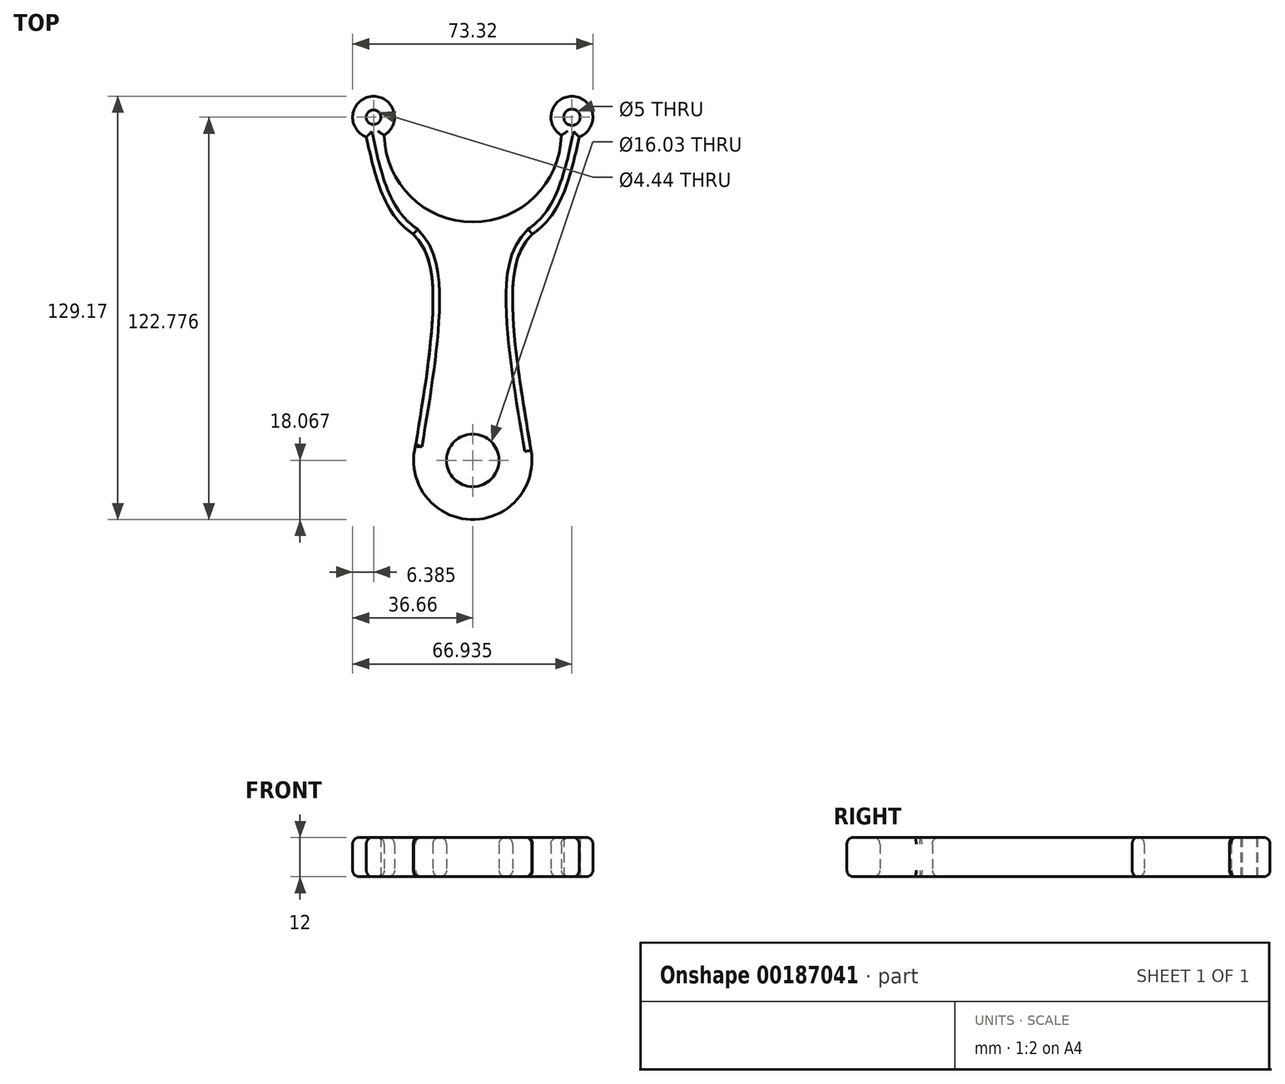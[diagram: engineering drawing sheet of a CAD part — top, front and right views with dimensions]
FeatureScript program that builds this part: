
annotation { "Feature Type Name" : "Feature", "Feature Type Description" : "" }
export const myFeature = defineFeature(function(context is Context, id is Id, definition is map)
    precondition{}
    {
        {
            var Q0;
            Q0=qCreatedBy(makeId("Top.planeOp"),FACE);
            var sketch = newSketch(context, id + "F0", { "sketchPlane" : qUnion([Q0])});
            skArc(sketch, "E0", {"start": v(-27, 0) * mm, "mid": v(-0.25, -27) * mm, "end": v(27, -0.5) * mm});
            skLineSegment(sketch, "E1", {"start": v(0, 0) * mm, "end": v(0, 27) * mm, "construction": true});
            skLineSegment(sketch, "E2", {"start": v(0, 0) * mm, "end": v(0, -27) * mm, "construction": true});
            skLineSegment(sketch, "E3", {"start": v(0, 0) * mm, "end": v(-27, 0) * mm});
            skLineSegment(sketch, "E4", {"start": v(-27, 0) * mm, "end": v(27, 0) * mm, "construction": true});
            skFitSpline(sketch, "E5", {"points": [v(0, -38.66) * mm, v(22.6, -26.79) * mm, v(32.7, 0) * mm], "startDerivative": vector(53.05, 17.73) * mm, "endDerivative": vector(12.73, 59.18) * mm});
            skFitSpline(sketch, "E6.MirrorCS", {"points": [v(0, -38.66) * mm, v(-22.6, -26.79) * mm, v(-32.7, 0) * mm], "startDerivative": vector(-53.05, 17.73) * mm, "endDerivative": vector(-12.73, 59.18) * mm});
            skArc(sketch, "E7", {"start": v(32.48, -1.01) * mm, "mid": v(30.87, 11.35) * mm, "end": v(27, -0.5) * mm});
            skArc(sketch, "E8", {"start": v(-17.48, -95.18) * mm, "mid": v(-0.76, -117.77) * mm, "end": v(17.8, -96.66) * mm});
            skArc(sketch, "E9.MirrorC", {"start": v(-32.48, -1.01) * mm, "mid": v(-30.87, 11.35) * mm, "end": v(-27, -0.5) * mm});
            skFitSpline(sketch, "E10", {"points": [v(22.6, -26.79) * mm, v(13.5, -38.66) * mm, v(17.82, -96.8) * mm], "startDerivative": vector(-32.69, -26.53) * mm, "endDerivative": vector(17.64, -104.94) * mm});
            skFitSpline(sketch, "E11", {"points": [v(-22.6, -26.79) * mm, v(-13.5, -38.66) * mm, v(-18, -98.3) * mm], "startDerivative": vector(32.95, -26.64) * mm, "endDerivative": vector(-18.1, -107.4) * mm});
            skCircle(sketch, "E12", {"center": v(0, -99.72) * mm, "radius": 8.02 * mm});
            skCircle(sketch, "E13", {"center": v(30.27, 4.99) * mm, "radius": 2.5 * mm});
            skCircle(sketch, "E14", {"center": v(-30.27, 4.99) * mm, "radius": 2.22 * mm});
            skSolve(sketch);
        }
        {
            var Q0;
            Q0 = qSketchRegion(id + "F0", true);
            extrude(context, id + "F1", {"entities" : qUnion([Q0]), "depth" : 12 * mm});
        }
        {
            var Q0;
            Q0=makeQuery(id+"F1.opExtrude","CAP_EDGE",EDGE,{"disambiguationData":[OSD([sQuery(id+"F0.wireOp",EDGE,"E10")])],"isStart":false});
            var Q1;
            Q1=makeQuery(id+"F1.opExtrude","CAP_EDGE",EDGE,{"disambiguationData":[OSD([sQuery(id+"F0.wireOp",EDGE,"E11")])],"isStart":false});
            var Q2;
            Q2=makeQuery(id+"F1.opExtrude","CAP_EDGE",EDGE,{"disambiguationData":[OSD([sQuery(id+"F0.wireOp",EDGE,"E8")])],"isStart":true});
            var Q3;
            Q3=makeQuery(id+"F1.opExtrude","CAP_EDGE",EDGE,{"disambiguationData":[OSD([sQuery(id+"F0.wireOp",EDGE,"E8")])],"isStart":false});
            var Q4;
            Q4=makeQuery(id+"F1.opExtrude","CAP_EDGE",EDGE,{"disambiguationData":[OSD([sQuery(id+"F0.wireOp",EDGE,"E0")])],"isStart":false});
            var Q5;
            Q5=makeQuery(id+"F1.opExtrude","CAP_EDGE",EDGE,{"disambiguationData":[OSD([sQuery(id+"F0.wireOp",EDGE,"E6.MirrorCS")])],"isStart":false});
            var Q6;
            Q6=makeQuery(id+"F1.opExtrude","CAP_EDGE",EDGE,{"disambiguationData":[OSD([sQuery(id+"F0.wireOp",EDGE,"E0")])],"isStart":true});
            var Q7;
            Q7=makeQuery(id+"F1.opExtrude","CAP_EDGE",EDGE,{"disambiguationData":[OSD([sQuery(id+"F0.wireOp",EDGE,"E5")])],"isStart":false});
            var Q8;
            Q8=makeQuery(id+"F1.opExtrude","CAP_EDGE",EDGE,{"disambiguationData":[OSD([sQuery(id+"F0.wireOp",EDGE,"E5")])],"isStart":true});
            var Q9;
            Q9=makeQuery(id+"F1.opExtrude","CAP_EDGE",EDGE,{"disambiguationData":[OSD([sQuery(id+"F0.wireOp",EDGE,"E10")])],"isStart":true});
            var Q10;
            Q10=makeQuery(id+"F1.opExtrude","CAP_EDGE",EDGE,{"disambiguationData":[OSD([sQuery(id+"F0.wireOp",EDGE,"E9.MirrorC")])],"isStart":false});
            var Q11;
            Q11=makeQuery(id+"F1.opExtrude","CAP_EDGE",EDGE,{"disambiguationData":[OSD([sQuery(id+"F0.wireOp",EDGE,"E9.MirrorC")])],"isStart":true});
            var Q12;
            Q12=makeQuery(id+"F1.opExtrude","CAP_EDGE",EDGE,{"disambiguationData":[OSD([sQuery(id+"F0.wireOp",EDGE,"E7")])],"isStart":false});
            var Q13;
            Q13=makeQuery(id+"F1.opExtrude","CAP_EDGE",EDGE,{"disambiguationData":[OSD([sQuery(id+"F0.wireOp",EDGE,"E7")])],"isStart":true});
            var Q14;
            Q14=makeQuery(id+"F1.opExtrude","CAP_EDGE",EDGE,{"disambiguationData":[OSD([sQuery(id+"F0.wireOp",EDGE,"E12")])],"isStart":false});
            var Q15;
            Q15=makeQuery(id+"F1.opExtrude","CAP_EDGE",EDGE,{"disambiguationData":[OSD([sQuery(id+"F0.wireOp",EDGE,"E12")])],"isStart":true});
            var Q16;
            Q16=makeQuery(id+"F1.opExtrude","CAP_EDGE",EDGE,{"disambiguationData":[OSD([sQuery(id+"F0.wireOp",EDGE,"E11")])],"isStart":true});
            var Q17;
            Q17=makeQuery(id+"F1.opExtrude","CAP_EDGE",EDGE,{"disambiguationData":[OSD([sQuery(id+"F0.wireOp",EDGE,"E6.MirrorCS")])],"isStart":true});
            fillet(context, id + "F2", {"entities" : qUnion([Q0, Q1, Q2, Q3, Q4, Q5, Q6, Q7, Q8, Q9, Q10, Q11, Q12, Q13, Q14, Q15, Q16, Q17]), "radius" : 2 * mm, "tangentPropagation" : true, "allowEdgeOverflow" : false});
        }
        {
            var Q0;
            {var subQ0=sQuery(id+"F0.wireOp",EDGE,"E10");Q0=makeQuery(id+"F2.opFillet","BLEND_EDGE",EDGE,{"blendedFrom":[makeQuery(id+"F1.opExtrude","CAP_EDGE",EDGE,{"disambiguationData":[OSD([subQ0])],"isStart":false}),makeQuery(id+"F1.opExtrude","CAP_FACE",FACE,{"disambiguationData":[OSD([sQuery(id+"F0.wireOp",EDGE,"E0"),sQuery(id+"F0.wireOp",EDGE,"E5"),sQuery(id+"F0.wireOp",EDGE,"E6.MirrorCS"),sQuery(id+"F0.wireOp",EDGE,"E7"),sQuery(id+"F0.wireOp",EDGE,"E8"),sQuery(id+"F0.wireOp",EDGE,"E9.MirrorC"),subQ0,sQuery(id+"F0.wireOp",EDGE,"E11"),sQuery(id+"F0.wireOp",EDGE,"E12"),sQuery(id+"F0.wireOp",EDGE,"E13"),sQuery(id+"F0.wireOp",EDGE,"E14")])],"isStart":false})],"blendedInto":[makeQuery(id+"F1.opExtrude","CAP_FACE",FACE,{"disambiguationData":[OSD([sQuery(id+"F0.wireOp",EDGE,"E0"),sQuery(id+"F0.wireOp",EDGE,"E5"),sQuery(id+"F0.wireOp",EDGE,"E6.MirrorCS"),sQuery(id+"F0.wireOp",EDGE,"E7"),sQuery(id+"F0.wireOp",EDGE,"E8"),sQuery(id+"F0.wireOp",EDGE,"E9.MirrorC"),subQ0,sQuery(id+"F0.wireOp",EDGE,"E11"),sQuery(id+"F0.wireOp",EDGE,"E12"),sQuery(id+"F0.wireOp",EDGE,"E13"),sQuery(id+"F0.wireOp",EDGE,"E14")])],"isStart":false})]});}
            var Q1;
            {var subQ0=sQuery(id+"F0.wireOp",EDGE,"E8");Q1=makeQuery(id+"F2.opFillet","BLEND_FACE",FACE,{"disambiguationData":[OSD([subQ0]),TDD([makeQuery(id+"F1.opExtrude","CAP_EDGE",EDGE,{"disambiguationData":[OSD([subQ0])],"isStart":false})])]});}
            var Q2;
            {var subQ0=sQuery(id+"F0.wireOp",EDGE,"E0");Q2=makeQuery(id+"F2.opFillet","BLEND_EDGE",EDGE,{"blendedFrom":[makeQuery(id+"F1.opExtrude","CAP_EDGE",EDGE,{"disambiguationData":[OSD([subQ0])],"isStart":false}),makeQuery(id+"F1.opExtrude","CAP_FACE",FACE,{"disambiguationData":[OSD([subQ0,sQuery(id+"F0.wireOp",EDGE,"E5"),sQuery(id+"F0.wireOp",EDGE,"E6.MirrorCS"),sQuery(id+"F0.wireOp",EDGE,"E7"),sQuery(id+"F0.wireOp",EDGE,"E8"),sQuery(id+"F0.wireOp",EDGE,"E9.MirrorC"),sQuery(id+"F0.wireOp",EDGE,"E10"),sQuery(id+"F0.wireOp",EDGE,"E11"),sQuery(id+"F0.wireOp",EDGE,"E12"),sQuery(id+"F0.wireOp",EDGE,"E13"),sQuery(id+"F0.wireOp",EDGE,"E14")])],"isStart":false})],"blendedInto":[makeQuery(id+"F1.opExtrude","CAP_FACE",FACE,{"disambiguationData":[OSD([subQ0,sQuery(id+"F0.wireOp",EDGE,"E5"),sQuery(id+"F0.wireOp",EDGE,"E6.MirrorCS"),sQuery(id+"F0.wireOp",EDGE,"E7"),sQuery(id+"F0.wireOp",EDGE,"E8"),sQuery(id+"F0.wireOp",EDGE,"E9.MirrorC"),sQuery(id+"F0.wireOp",EDGE,"E10"),sQuery(id+"F0.wireOp",EDGE,"E11"),sQuery(id+"F0.wireOp",EDGE,"E12"),sQuery(id+"F0.wireOp",EDGE,"E13"),sQuery(id+"F0.wireOp",EDGE,"E14")])],"isStart":false})]});}
            var Q3;
            {var subQ0=sQuery(id+"F0.wireOp",EDGE,"E11");Q3=makeQuery(id+"F2.opFillet","BLEND_EDGE",EDGE,{"blendedFrom":[makeQuery(id+"F1.opExtrude","CAP_EDGE",EDGE,{"disambiguationData":[OSD([subQ0])],"isStart":false}),makeQuery(id+"F1.opExtrude","CAP_FACE",FACE,{"disambiguationData":[OSD([sQuery(id+"F0.wireOp",EDGE,"E0"),sQuery(id+"F0.wireOp",EDGE,"E5"),sQuery(id+"F0.wireOp",EDGE,"E6.MirrorCS"),sQuery(id+"F0.wireOp",EDGE,"E7"),sQuery(id+"F0.wireOp",EDGE,"E8"),sQuery(id+"F0.wireOp",EDGE,"E9.MirrorC"),sQuery(id+"F0.wireOp",EDGE,"E10"),subQ0,sQuery(id+"F0.wireOp",EDGE,"E12"),sQuery(id+"F0.wireOp",EDGE,"E13"),sQuery(id+"F0.wireOp",EDGE,"E14")])],"isStart":false})],"blendedInto":[makeQuery(id+"F1.opExtrude","CAP_FACE",FACE,{"disambiguationData":[OSD([sQuery(id+"F0.wireOp",EDGE,"E0"),sQuery(id+"F0.wireOp",EDGE,"E5"),sQuery(id+"F0.wireOp",EDGE,"E6.MirrorCS"),sQuery(id+"F0.wireOp",EDGE,"E7"),sQuery(id+"F0.wireOp",EDGE,"E8"),sQuery(id+"F0.wireOp",EDGE,"E9.MirrorC"),sQuery(id+"F0.wireOp",EDGE,"E10"),subQ0,sQuery(id+"F0.wireOp",EDGE,"E12"),sQuery(id+"F0.wireOp",EDGE,"E13"),sQuery(id+"F0.wireOp",EDGE,"E14")])],"isStart":false})]});}
            var Q4;
            {var subQ0=sQuery(id+"F0.wireOp",EDGE,"E8");Q4=makeQuery(id+"F2.opFillet","BLEND_EDGE",EDGE,{"blendedFrom":[makeQuery(id+"F1.opExtrude","CAP_EDGE",EDGE,{"disambiguationData":[OSD([subQ0])],"isStart":false}),makeQuery(id+"F1.opExtrude","CAP_FACE",FACE,{"disambiguationData":[OSD([sQuery(id+"F0.wireOp",EDGE,"E0"),sQuery(id+"F0.wireOp",EDGE,"E5"),sQuery(id+"F0.wireOp",EDGE,"E6.MirrorCS"),sQuery(id+"F0.wireOp",EDGE,"E7"),subQ0,sQuery(id+"F0.wireOp",EDGE,"E9.MirrorC"),sQuery(id+"F0.wireOp",EDGE,"E10"),sQuery(id+"F0.wireOp",EDGE,"E11"),sQuery(id+"F0.wireOp",EDGE,"E12"),sQuery(id+"F0.wireOp",EDGE,"E13"),sQuery(id+"F0.wireOp",EDGE,"E14")])],"isStart":false})],"blendedInto":[makeQuery(id+"F1.opExtrude","CAP_FACE",FACE,{"disambiguationData":[OSD([sQuery(id+"F0.wireOp",EDGE,"E0"),sQuery(id+"F0.wireOp",EDGE,"E5"),sQuery(id+"F0.wireOp",EDGE,"E6.MirrorCS"),sQuery(id+"F0.wireOp",EDGE,"E7"),subQ0,sQuery(id+"F0.wireOp",EDGE,"E9.MirrorC"),sQuery(id+"F0.wireOp",EDGE,"E10"),sQuery(id+"F0.wireOp",EDGE,"E11"),sQuery(id+"F0.wireOp",EDGE,"E12"),sQuery(id+"F0.wireOp",EDGE,"E13"),sQuery(id+"F0.wireOp",EDGE,"E14")])],"isStart":false})]});}
            var Q5;
            {var subQ0=sQuery(id+"F0.wireOp",EDGE,"E8");Q5=makeQuery(id+"F2.opFillet","BLEND_EDGE",EDGE,{"blendedFrom":[makeQuery(id+"F1.opExtrude","CAP_EDGE",EDGE,{"disambiguationData":[OSD([subQ0])],"isStart":false}),makeQuery(id+"F1.opExtrude","SWEPT_FACE",FACE,{"disambiguationData":[OSD([subQ0])]})],"blendedInto":[makeQuery(id+"F1.opExtrude","SWEPT_FACE",FACE,{"disambiguationData":[OSD([subQ0])]})]});}
            var Q6;
            {var subQ0=sQuery(id+"F0.wireOp",EDGE,"E12");Q6=makeQuery(id+"F2.opFillet","BLEND_EDGE",EDGE,{"blendedFrom":[makeQuery(id+"F1.opExtrude","CAP_EDGE",EDGE,{"disambiguationData":[OSD([subQ0])],"isStart":false}),makeQuery(id+"F1.opExtrude","CAP_FACE",FACE,{"disambiguationData":[OSD([sQuery(id+"F0.wireOp",EDGE,"E0"),sQuery(id+"F0.wireOp",EDGE,"E5"),sQuery(id+"F0.wireOp",EDGE,"E6.MirrorCS"),sQuery(id+"F0.wireOp",EDGE,"E7"),sQuery(id+"F0.wireOp",EDGE,"E8"),sQuery(id+"F0.wireOp",EDGE,"E9.MirrorC"),sQuery(id+"F0.wireOp",EDGE,"E10"),sQuery(id+"F0.wireOp",EDGE,"E11"),subQ0,sQuery(id+"F0.wireOp",EDGE,"E13"),sQuery(id+"F0.wireOp",EDGE,"E14")])],"isStart":false})],"blendedInto":[makeQuery(id+"F1.opExtrude","CAP_FACE",FACE,{"disambiguationData":[OSD([sQuery(id+"F0.wireOp",EDGE,"E0"),sQuery(id+"F0.wireOp",EDGE,"E5"),sQuery(id+"F0.wireOp",EDGE,"E6.MirrorCS"),sQuery(id+"F0.wireOp",EDGE,"E7"),sQuery(id+"F0.wireOp",EDGE,"E8"),sQuery(id+"F0.wireOp",EDGE,"E9.MirrorC"),sQuery(id+"F0.wireOp",EDGE,"E10"),sQuery(id+"F0.wireOp",EDGE,"E11"),subQ0,sQuery(id+"F0.wireOp",EDGE,"E13"),sQuery(id+"F0.wireOp",EDGE,"E14")])],"isStart":false})]});}
            var Q7;
            {var subQ0=sQuery(id+"F0.wireOp",EDGE,"E12");Q7=makeQuery(id+"F2.opFillet","BLEND_EDGE",EDGE,{"blendedFrom":[makeQuery(id+"F1.opExtrude","CAP_EDGE",EDGE,{"disambiguationData":[OSD([subQ0])],"isStart":false}),makeQuery(id+"F1.opExtrude","SWEPT_FACE",FACE,{"disambiguationData":[OSD([subQ0])]})],"blendedInto":[makeQuery(id+"F1.opExtrude","SWEPT_FACE",FACE,{"disambiguationData":[OSD([subQ0])]})]});}
            var Q8;
            {var subQ0=sQuery(id+"F0.wireOp",EDGE,"E5");Q8=makeQuery(id+"F2.opFillet","BLEND_EDGE",EDGE,{"blendedFrom":[makeQuery(id+"F1.opExtrude","CAP_EDGE",EDGE,{"disambiguationData":[OSD([subQ0])],"isStart":false}),makeQuery(id+"F1.opExtrude","CAP_FACE",FACE,{"disambiguationData":[OSD([sQuery(id+"F0.wireOp",EDGE,"E0"),subQ0,sQuery(id+"F0.wireOp",EDGE,"E6.MirrorCS"),sQuery(id+"F0.wireOp",EDGE,"E7"),sQuery(id+"F0.wireOp",EDGE,"E8"),sQuery(id+"F0.wireOp",EDGE,"E9.MirrorC"),sQuery(id+"F0.wireOp",EDGE,"E10"),sQuery(id+"F0.wireOp",EDGE,"E11"),sQuery(id+"F0.wireOp",EDGE,"E12"),sQuery(id+"F0.wireOp",EDGE,"E13"),sQuery(id+"F0.wireOp",EDGE,"E14")])],"isStart":false})],"blendedInto":[makeQuery(id+"F1.opExtrude","CAP_FACE",FACE,{"disambiguationData":[OSD([sQuery(id+"F0.wireOp",EDGE,"E0"),subQ0,sQuery(id+"F0.wireOp",EDGE,"E6.MirrorCS"),sQuery(id+"F0.wireOp",EDGE,"E7"),sQuery(id+"F0.wireOp",EDGE,"E8"),sQuery(id+"F0.wireOp",EDGE,"E9.MirrorC"),sQuery(id+"F0.wireOp",EDGE,"E10"),sQuery(id+"F0.wireOp",EDGE,"E11"),sQuery(id+"F0.wireOp",EDGE,"E12"),sQuery(id+"F0.wireOp",EDGE,"E13"),sQuery(id+"F0.wireOp",EDGE,"E14")])],"isStart":false})]});}
            var Q9;
            {var subQ0=sQuery(id+"F0.wireOp",EDGE,"E10");Q9=makeQuery(id+"F2.opFillet","BLEND_EDGE",EDGE,{"blendedFrom":[makeQuery(id+"F1.opExtrude","CAP_EDGE",EDGE,{"disambiguationData":[OSD([subQ0])],"isStart":true}),makeQuery(id+"F1.opExtrude","SWEPT_FACE",FACE,{"disambiguationData":[OSD([subQ0])]})],"blendedInto":[makeQuery(id+"F1.opExtrude","SWEPT_FACE",FACE,{"disambiguationData":[OSD([subQ0])]})]});}
            var Q10;
            {var subQ0=sQuery(id+"F0.wireOp",EDGE,"E10");Q10=makeQuery(id+"F2.opFillet","BLEND_EDGE",EDGE,{"blendedFrom":[makeQuery(id+"F1.opExtrude","CAP_EDGE",EDGE,{"disambiguationData":[OSD([subQ0])],"isStart":false}),makeQuery(id+"F1.opExtrude","SWEPT_FACE",FACE,{"disambiguationData":[OSD([subQ0])]})],"blendedInto":[makeQuery(id+"F1.opExtrude","SWEPT_FACE",FACE,{"disambiguationData":[OSD([subQ0])]})]});}
            var Q11;
            {var subQ0=sQuery(id+"F0.wireOp",EDGE,"E5");Q11=makeQuery(id+"F2.opFillet","BLEND_EDGE",EDGE,{"blendedFrom":[makeQuery(id+"F1.opExtrude","CAP_EDGE",EDGE,{"disambiguationData":[OSD([subQ0])],"isStart":false}),makeQuery(id+"F1.opExtrude","SWEPT_FACE",FACE,{"disambiguationData":[OSD([subQ0])]})],"blendedInto":[makeQuery(id+"F1.opExtrude","SWEPT_FACE",FACE,{"disambiguationData":[OSD([subQ0])]})]});}
            var Q12;
            {var subQ0=sQuery(id+"F0.wireOp",EDGE,"E5");Q12=makeQuery(id+"F2.opFillet","BLEND_EDGE",EDGE,{"blendedFrom":[makeQuery(id+"F1.opExtrude","CAP_EDGE",EDGE,{"disambiguationData":[OSD([subQ0])],"isStart":true}),makeQuery(id+"F1.opExtrude","SWEPT_FACE",FACE,{"disambiguationData":[OSD([subQ0])]})],"blendedInto":[makeQuery(id+"F1.opExtrude","SWEPT_FACE",FACE,{"disambiguationData":[OSD([subQ0])]})]});}
            var Q13;
            {var subQ0=sQuery(id+"F0.wireOp",EDGE,"E0");Q13=makeQuery(id+"F2.opFillet","BLEND_EDGE",EDGE,{"blendedFrom":[makeQuery(id+"F1.opExtrude","CAP_EDGE",EDGE,{"disambiguationData":[OSD([subQ0])],"isStart":false}),makeQuery(id+"F1.opExtrude","SWEPT_FACE",FACE,{"disambiguationData":[OSD([subQ0])]})],"blendedInto":[makeQuery(id+"F1.opExtrude","SWEPT_FACE",FACE,{"disambiguationData":[OSD([subQ0])]})]});}
            var Q14;
            {var subQ0=sQuery(id+"F0.wireOp",EDGE,"E0");Q14=makeQuery(id+"F2.opFillet","BLEND_EDGE",EDGE,{"blendedFrom":[makeQuery(id+"F1.opExtrude","CAP_EDGE",EDGE,{"disambiguationData":[OSD([subQ0])],"isStart":true}),makeQuery(id+"F1.opExtrude","SWEPT_FACE",FACE,{"disambiguationData":[OSD([subQ0])]})],"blendedInto":[makeQuery(id+"F1.opExtrude","SWEPT_FACE",FACE,{"disambiguationData":[OSD([subQ0])]})]});}
            var Q15;
            {var subQ0=sQuery(id+"F0.wireOp",EDGE,"E9.MirrorC");Q15=makeQuery(id+"F2.opFillet","BLEND_EDGE",EDGE,{"blendedFrom":[makeQuery(id+"F1.opExtrude","CAP_EDGE",EDGE,{"disambiguationData":[OSD([subQ0])],"isStart":true}),makeQuery(id+"F1.opExtrude","SWEPT_FACE",FACE,{"disambiguationData":[OSD([subQ0])]})],"blendedInto":[makeQuery(id+"F1.opExtrude","SWEPT_FACE",FACE,{"disambiguationData":[OSD([subQ0])]})]});}
            var Q16;
            {var subQ0=sQuery(id+"F0.wireOp",EDGE,"E0");Q16=makeQuery(id+"F2.opFillet","BLEND_EDGE",EDGE,{"blendedFrom":[makeQuery(id+"F1.opExtrude","CAP_EDGE",EDGE,{"disambiguationData":[OSD([subQ0])],"isStart":true}),makeQuery(id+"F1.opExtrude","CAP_FACE",FACE,{"disambiguationData":[OSD([subQ0,sQuery(id+"F0.wireOp",EDGE,"E5"),sQuery(id+"F0.wireOp",EDGE,"E6.MirrorCS"),sQuery(id+"F0.wireOp",EDGE,"E7"),sQuery(id+"F0.wireOp",EDGE,"E8"),sQuery(id+"F0.wireOp",EDGE,"E9.MirrorC"),sQuery(id+"F0.wireOp",EDGE,"E10"),sQuery(id+"F0.wireOp",EDGE,"E11"),sQuery(id+"F0.wireOp",EDGE,"E12"),sQuery(id+"F0.wireOp",EDGE,"E13"),sQuery(id+"F0.wireOp",EDGE,"E14")])],"isStart":true})],"blendedInto":[makeQuery(id+"F1.opExtrude","CAP_FACE",FACE,{"disambiguationData":[OSD([subQ0,sQuery(id+"F0.wireOp",EDGE,"E5"),sQuery(id+"F0.wireOp",EDGE,"E6.MirrorCS"),sQuery(id+"F0.wireOp",EDGE,"E7"),sQuery(id+"F0.wireOp",EDGE,"E8"),sQuery(id+"F0.wireOp",EDGE,"E9.MirrorC"),sQuery(id+"F0.wireOp",EDGE,"E10"),sQuery(id+"F0.wireOp",EDGE,"E11"),sQuery(id+"F0.wireOp",EDGE,"E12"),sQuery(id+"F0.wireOp",EDGE,"E13"),sQuery(id+"F0.wireOp",EDGE,"E14")])],"isStart":true})]});}
            var Q17;
            {var subQ0=sQuery(id+"F0.wireOp",EDGE,"E11");Q17=makeQuery(id+"F2.opFillet","BLEND_EDGE",EDGE,{"blendedFrom":[makeQuery(id+"F1.opExtrude","CAP_EDGE",EDGE,{"disambiguationData":[OSD([subQ0])],"isStart":true}),makeQuery(id+"F1.opExtrude","CAP_FACE",FACE,{"disambiguationData":[OSD([sQuery(id+"F0.wireOp",EDGE,"E0"),sQuery(id+"F0.wireOp",EDGE,"E5"),sQuery(id+"F0.wireOp",EDGE,"E6.MirrorCS"),sQuery(id+"F0.wireOp",EDGE,"E7"),sQuery(id+"F0.wireOp",EDGE,"E8"),sQuery(id+"F0.wireOp",EDGE,"E9.MirrorC"),sQuery(id+"F0.wireOp",EDGE,"E10"),subQ0,sQuery(id+"F0.wireOp",EDGE,"E12"),sQuery(id+"F0.wireOp",EDGE,"E13"),sQuery(id+"F0.wireOp",EDGE,"E14")])],"isStart":true})],"blendedInto":[makeQuery(id+"F1.opExtrude","CAP_FACE",FACE,{"disambiguationData":[OSD([sQuery(id+"F0.wireOp",EDGE,"E0"),sQuery(id+"F0.wireOp",EDGE,"E5"),sQuery(id+"F0.wireOp",EDGE,"E6.MirrorCS"),sQuery(id+"F0.wireOp",EDGE,"E7"),sQuery(id+"F0.wireOp",EDGE,"E8"),sQuery(id+"F0.wireOp",EDGE,"E9.MirrorC"),sQuery(id+"F0.wireOp",EDGE,"E10"),subQ0,sQuery(id+"F0.wireOp",EDGE,"E12"),sQuery(id+"F0.wireOp",EDGE,"E13"),sQuery(id+"F0.wireOp",EDGE,"E14")])],"isStart":true})]});}
            var Q18;
            {var subQ0=sQuery(id+"F0.wireOp",EDGE,"E11");Q18=makeQuery(id+"F2.opFillet","BLEND_EDGE",EDGE,{"blendedFrom":[makeQuery(id+"F1.opExtrude","CAP_EDGE",EDGE,{"disambiguationData":[OSD([subQ0])],"isStart":false}),makeQuery(id+"F1.opExtrude","SWEPT_FACE",FACE,{"disambiguationData":[OSD([subQ0])]})],"blendedInto":[makeQuery(id+"F1.opExtrude","SWEPT_FACE",FACE,{"disambiguationData":[OSD([subQ0])]})]});}
            var Q19;
            {var subQ0=sQuery(id+"F0.wireOp",EDGE,"E6.MirrorCS");Q19=makeQuery(id+"F2.opFillet","BLEND_EDGE",EDGE,{"blendedFrom":[makeQuery(id+"F1.opExtrude","CAP_EDGE",EDGE,{"disambiguationData":[OSD([subQ0])],"isStart":false}),makeQuery(id+"F1.opExtrude","SWEPT_FACE",FACE,{"disambiguationData":[OSD([subQ0])]})],"blendedInto":[makeQuery(id+"F1.opExtrude","SWEPT_FACE",FACE,{"disambiguationData":[OSD([subQ0])]})]});}
            var Q20;
            {var subQ0=sQuery(id+"F0.wireOp",EDGE,"E6.MirrorCS");Q20=makeQuery(id+"F2.opFillet","BLEND_EDGE",EDGE,{"blendedFrom":[makeQuery(id+"F1.opExtrude","CAP_EDGE",EDGE,{"disambiguationData":[OSD([subQ0])],"isStart":false}),makeQuery(id+"F1.opExtrude","CAP_FACE",FACE,{"disambiguationData":[OSD([sQuery(id+"F0.wireOp",EDGE,"E0"),sQuery(id+"F0.wireOp",EDGE,"E5"),subQ0,sQuery(id+"F0.wireOp",EDGE,"E7"),sQuery(id+"F0.wireOp",EDGE,"E8"),sQuery(id+"F0.wireOp",EDGE,"E9.MirrorC"),sQuery(id+"F0.wireOp",EDGE,"E10"),sQuery(id+"F0.wireOp",EDGE,"E11"),sQuery(id+"F0.wireOp",EDGE,"E12"),sQuery(id+"F0.wireOp",EDGE,"E13"),sQuery(id+"F0.wireOp",EDGE,"E14")])],"isStart":false})],"blendedInto":[makeQuery(id+"F1.opExtrude","CAP_FACE",FACE,{"disambiguationData":[OSD([sQuery(id+"F0.wireOp",EDGE,"E0"),sQuery(id+"F0.wireOp",EDGE,"E5"),subQ0,sQuery(id+"F0.wireOp",EDGE,"E7"),sQuery(id+"F0.wireOp",EDGE,"E8"),sQuery(id+"F0.wireOp",EDGE,"E9.MirrorC"),sQuery(id+"F0.wireOp",EDGE,"E10"),sQuery(id+"F0.wireOp",EDGE,"E11"),sQuery(id+"F0.wireOp",EDGE,"E12"),sQuery(id+"F0.wireOp",EDGE,"E13"),sQuery(id+"F0.wireOp",EDGE,"E14")])],"isStart":false})]});}
            var Q21;
            {var subQ0=sQuery(id+"F0.wireOp",EDGE,"E9.MirrorC");Q21=makeQuery(id+"F2.opFillet","BLEND_EDGE",EDGE,{"blendedFrom":[makeQuery(id+"F1.opExtrude","CAP_EDGE",EDGE,{"disambiguationData":[OSD([subQ0])],"isStart":false}),makeQuery(id+"F1.opExtrude","SWEPT_FACE",FACE,{"disambiguationData":[OSD([subQ0])]})],"blendedInto":[makeQuery(id+"F1.opExtrude","SWEPT_FACE",FACE,{"disambiguationData":[OSD([subQ0])]})]});}
            var Q22;
            {var subQ0=sQuery(id+"F0.wireOp",EDGE,"E7");Q22=makeQuery(id+"F2.opFillet","BLEND_EDGE",EDGE,{"blendedFrom":[makeQuery(id+"F1.opExtrude","CAP_EDGE",EDGE,{"disambiguationData":[OSD([subQ0])],"isStart":false}),makeQuery(id+"F1.opExtrude","SWEPT_FACE",FACE,{"disambiguationData":[OSD([subQ0])]})],"blendedInto":[makeQuery(id+"F1.opExtrude","SWEPT_FACE",FACE,{"disambiguationData":[OSD([subQ0])]})]});}
            var Q23;
            {var subQ0=sQuery(id+"F0.wireOp",EDGE,"E7");Q23=makeQuery(id+"F2.opFillet","BLEND_EDGE",EDGE,{"blendedFrom":[makeQuery(id+"F1.opExtrude","CAP_EDGE",EDGE,{"disambiguationData":[OSD([subQ0])],"isStart":true}),makeQuery(id+"F1.opExtrude","SWEPT_FACE",FACE,{"disambiguationData":[OSD([subQ0])]})],"blendedInto":[makeQuery(id+"F1.opExtrude","SWEPT_FACE",FACE,{"disambiguationData":[OSD([subQ0])]})]});}
            var Q24;
            {var subQ0=sQuery(id+"F0.wireOp",EDGE,"E6.MirrorCS");Q24=makeQuery(id+"F2.opFillet","BLEND_EDGE",EDGE,{"blendedFrom":[makeQuery(id+"F1.opExtrude","CAP_EDGE",EDGE,{"disambiguationData":[OSD([subQ0])],"isStart":true}),makeQuery(id+"F1.opExtrude","SWEPT_FACE",FACE,{"disambiguationData":[OSD([subQ0])]})],"blendedInto":[makeQuery(id+"F1.opExtrude","SWEPT_FACE",FACE,{"disambiguationData":[OSD([subQ0])]})]});}
            var Q25;
            {var subQ0=sQuery(id+"F0.wireOp",EDGE,"E6.MirrorCS");Q25=makeQuery(id+"F2.opFillet","BLEND_EDGE",EDGE,{"blendedFrom":[makeQuery(id+"F1.opExtrude","CAP_EDGE",EDGE,{"disambiguationData":[OSD([subQ0])],"isStart":true}),makeQuery(id+"F1.opExtrude","CAP_FACE",FACE,{"disambiguationData":[OSD([sQuery(id+"F0.wireOp",EDGE,"E0"),sQuery(id+"F0.wireOp",EDGE,"E5"),subQ0,sQuery(id+"F0.wireOp",EDGE,"E7"),sQuery(id+"F0.wireOp",EDGE,"E8"),sQuery(id+"F0.wireOp",EDGE,"E9.MirrorC"),sQuery(id+"F0.wireOp",EDGE,"E10"),sQuery(id+"F0.wireOp",EDGE,"E11"),sQuery(id+"F0.wireOp",EDGE,"E12"),sQuery(id+"F0.wireOp",EDGE,"E13"),sQuery(id+"F0.wireOp",EDGE,"E14")])],"isStart":true})],"blendedInto":[makeQuery(id+"F1.opExtrude","CAP_FACE",FACE,{"disambiguationData":[OSD([sQuery(id+"F0.wireOp",EDGE,"E0"),sQuery(id+"F0.wireOp",EDGE,"E5"),subQ0,sQuery(id+"F0.wireOp",EDGE,"E7"),sQuery(id+"F0.wireOp",EDGE,"E8"),sQuery(id+"F0.wireOp",EDGE,"E9.MirrorC"),sQuery(id+"F0.wireOp",EDGE,"E10"),sQuery(id+"F0.wireOp",EDGE,"E11"),sQuery(id+"F0.wireOp",EDGE,"E12"),sQuery(id+"F0.wireOp",EDGE,"E13"),sQuery(id+"F0.wireOp",EDGE,"E14")])],"isStart":true})]});}
            var Q26;
            {var subQ0=sQuery(id+"F0.wireOp",EDGE,"E11");Q26=makeQuery(id+"F2.opFillet","BLEND_EDGE",EDGE,{"blendedFrom":[makeQuery(id+"F1.opExtrude","CAP_EDGE",EDGE,{"disambiguationData":[OSD([subQ0])],"isStart":true}),makeQuery(id+"F1.opExtrude","SWEPT_FACE",FACE,{"disambiguationData":[OSD([subQ0])]})],"blendedInto":[makeQuery(id+"F1.opExtrude","SWEPT_FACE",FACE,{"disambiguationData":[OSD([subQ0])]})]});}
            var Q27;
            {var subQ0=sQuery(id+"F0.wireOp",EDGE,"E10");Q27=makeQuery(id+"F2.opFillet","BLEND_EDGE",EDGE,{"blendedFrom":[makeQuery(id+"F1.opExtrude","CAP_EDGE",EDGE,{"disambiguationData":[OSD([subQ0])],"isStart":true}),makeQuery(id+"F1.opExtrude","CAP_FACE",FACE,{"disambiguationData":[OSD([sQuery(id+"F0.wireOp",EDGE,"E0"),sQuery(id+"F0.wireOp",EDGE,"E5"),sQuery(id+"F0.wireOp",EDGE,"E6.MirrorCS"),sQuery(id+"F0.wireOp",EDGE,"E7"),sQuery(id+"F0.wireOp",EDGE,"E8"),sQuery(id+"F0.wireOp",EDGE,"E9.MirrorC"),subQ0,sQuery(id+"F0.wireOp",EDGE,"E11"),sQuery(id+"F0.wireOp",EDGE,"E12"),sQuery(id+"F0.wireOp",EDGE,"E13"),sQuery(id+"F0.wireOp",EDGE,"E14")])],"isStart":true})],"blendedInto":[makeQuery(id+"F1.opExtrude","CAP_FACE",FACE,{"disambiguationData":[OSD([sQuery(id+"F0.wireOp",EDGE,"E0"),sQuery(id+"F0.wireOp",EDGE,"E5"),sQuery(id+"F0.wireOp",EDGE,"E6.MirrorCS"),sQuery(id+"F0.wireOp",EDGE,"E7"),sQuery(id+"F0.wireOp",EDGE,"E8"),sQuery(id+"F0.wireOp",EDGE,"E9.MirrorC"),subQ0,sQuery(id+"F0.wireOp",EDGE,"E11"),sQuery(id+"F0.wireOp",EDGE,"E12"),sQuery(id+"F0.wireOp",EDGE,"E13"),sQuery(id+"F0.wireOp",EDGE,"E14")])],"isStart":true})]});}
            var Q28;
            {var subQ0=sQuery(id+"F0.wireOp",EDGE,"E8");Q28=makeQuery(id+"F2.opFillet","BLEND_EDGE",EDGE,{"blendedFrom":[makeQuery(id+"F1.opExtrude","CAP_EDGE",EDGE,{"disambiguationData":[OSD([subQ0])],"isStart":true}),makeQuery(id+"F1.opExtrude","SWEPT_FACE",FACE,{"disambiguationData":[OSD([subQ0])]})],"blendedInto":[makeQuery(id+"F1.opExtrude","SWEPT_FACE",FACE,{"disambiguationData":[OSD([subQ0])]})]});}
            var Q29;
            {var subQ0=sQuery(id+"F0.wireOp",EDGE,"E12");Q29=makeQuery(id+"F2.opFillet","BLEND_EDGE",EDGE,{"blendedFrom":[makeQuery(id+"F1.opExtrude","CAP_EDGE",EDGE,{"disambiguationData":[OSD([subQ0])],"isStart":true}),makeQuery(id+"F1.opExtrude","CAP_FACE",FACE,{"disambiguationData":[OSD([sQuery(id+"F0.wireOp",EDGE,"E0"),sQuery(id+"F0.wireOp",EDGE,"E5"),sQuery(id+"F0.wireOp",EDGE,"E6.MirrorCS"),sQuery(id+"F0.wireOp",EDGE,"E7"),sQuery(id+"F0.wireOp",EDGE,"E8"),sQuery(id+"F0.wireOp",EDGE,"E9.MirrorC"),sQuery(id+"F0.wireOp",EDGE,"E10"),sQuery(id+"F0.wireOp",EDGE,"E11"),subQ0,sQuery(id+"F0.wireOp",EDGE,"E13"),sQuery(id+"F0.wireOp",EDGE,"E14")])],"isStart":true})],"blendedInto":[makeQuery(id+"F1.opExtrude","CAP_FACE",FACE,{"disambiguationData":[OSD([sQuery(id+"F0.wireOp",EDGE,"E0"),sQuery(id+"F0.wireOp",EDGE,"E5"),sQuery(id+"F0.wireOp",EDGE,"E6.MirrorCS"),sQuery(id+"F0.wireOp",EDGE,"E7"),sQuery(id+"F0.wireOp",EDGE,"E8"),sQuery(id+"F0.wireOp",EDGE,"E9.MirrorC"),sQuery(id+"F0.wireOp",EDGE,"E10"),sQuery(id+"F0.wireOp",EDGE,"E11"),subQ0,sQuery(id+"F0.wireOp",EDGE,"E13"),sQuery(id+"F0.wireOp",EDGE,"E14")])],"isStart":true})]});}
            var Q30;
            {var subQ0=sQuery(id+"F0.wireOp",EDGE,"E12");Q30=makeQuery(id+"F2.opFillet","BLEND_EDGE",EDGE,{"blendedFrom":[makeQuery(id+"F1.opExtrude","CAP_EDGE",EDGE,{"disambiguationData":[OSD([subQ0])],"isStart":true}),makeQuery(id+"F1.opExtrude","SWEPT_FACE",FACE,{"disambiguationData":[OSD([subQ0])]})],"blendedInto":[makeQuery(id+"F1.opExtrude","SWEPT_FACE",FACE,{"disambiguationData":[OSD([subQ0])]})]});}
            var Q31;
            {var subQ0=sQuery(id+"F0.wireOp",EDGE,"E8");Q31=makeQuery(id+"F2.opFillet","BLEND_EDGE",EDGE,{"blendedFrom":[makeQuery(id+"F1.opExtrude","CAP_EDGE",EDGE,{"disambiguationData":[OSD([subQ0])],"isStart":true}),makeQuery(id+"F1.opExtrude","CAP_FACE",FACE,{"disambiguationData":[OSD([sQuery(id+"F0.wireOp",EDGE,"E0"),sQuery(id+"F0.wireOp",EDGE,"E5"),sQuery(id+"F0.wireOp",EDGE,"E6.MirrorCS"),sQuery(id+"F0.wireOp",EDGE,"E7"),subQ0,sQuery(id+"F0.wireOp",EDGE,"E9.MirrorC"),sQuery(id+"F0.wireOp",EDGE,"E10"),sQuery(id+"F0.wireOp",EDGE,"E11"),sQuery(id+"F0.wireOp",EDGE,"E12"),sQuery(id+"F0.wireOp",EDGE,"E13"),sQuery(id+"F0.wireOp",EDGE,"E14")])],"isStart":true})],"blendedInto":[makeQuery(id+"F1.opExtrude","CAP_FACE",FACE,{"disambiguationData":[OSD([sQuery(id+"F0.wireOp",EDGE,"E0"),sQuery(id+"F0.wireOp",EDGE,"E5"),sQuery(id+"F0.wireOp",EDGE,"E6.MirrorCS"),sQuery(id+"F0.wireOp",EDGE,"E7"),subQ0,sQuery(id+"F0.wireOp",EDGE,"E9.MirrorC"),sQuery(id+"F0.wireOp",EDGE,"E10"),sQuery(id+"F0.wireOp",EDGE,"E11"),sQuery(id+"F0.wireOp",EDGE,"E12"),sQuery(id+"F0.wireOp",EDGE,"E13"),sQuery(id+"F0.wireOp",EDGE,"E14")])],"isStart":true})]});}
            fillet(context, id + "F3", {"entities" : qUnion([Q0, Q1, Q2, Q3, Q4, Q5, Q6, Q7, Q8, Q9, Q10, Q11, Q12, Q13, Q14, Q15, Q16, Q17, Q18, Q19, Q20, Q21, Q22, Q23, Q24, Q25, Q26, Q27, Q28, Q29, Q30, Q31]), "radius" : 8 * mm, "tangentPropagation" : true, "allowEdgeOverflow" : false});
        }
    });
